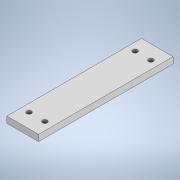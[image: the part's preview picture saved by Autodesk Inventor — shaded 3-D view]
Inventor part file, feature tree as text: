
AUTODESK INVENTOR PART (.ipt)
format: ipt  version: 2022 (Build 260153000, 153)  size: 111,616 bytes
history: native  units: mm
features: sketch x2, extrude x2, other x1, hole x1
ambient origin geometry x8: Origin, YZ Plane, XZ Plane, XY Plane, X Axis, Y Axis, Z Axis, Center Point
bodies: Body1 (feature_tree)
feature tree (6):
  other  "Sólido1"
  sketch  "Esboço1"  dims[d0=20.0mm d1=85.0mm]
  extrude  "Extrusão1"  Depth=85.0mm
  extrude  "Extrusão2"  Depth=4.0mm
  hole  "Furo1"  [1 undecoded]
  sketch  "Esboço2"  dims[d2=20.0mm d3=41.0mm d4=4.0mm d5=0.0mm d6=4.0mm d7=0.0mm d8=3.0mm d9=6.0mm d10=4.0mm d11=2.0mm d12=90.0deg d13=8.0mm d14=20.594885mm]
note: 1 required parameter value undecoded (feature->parameter linkage not recoverable at this tier; creation-order binding heuristic only, values carry confidence <= 0.55)
